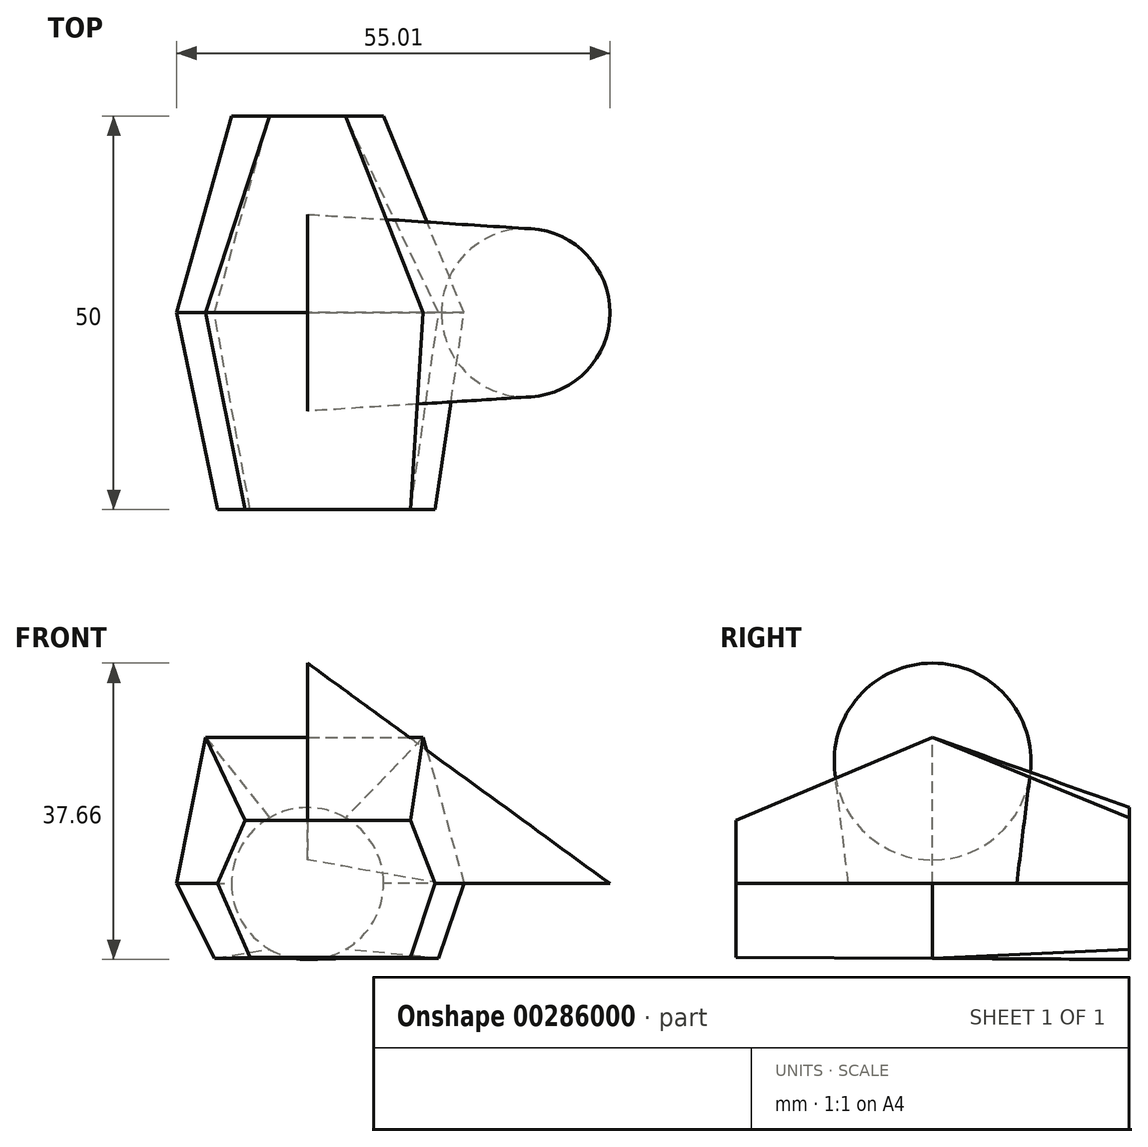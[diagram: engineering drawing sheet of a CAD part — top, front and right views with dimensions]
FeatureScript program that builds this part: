
annotation { "Feature Type Name" : "Feature", "Feature Type Description" : "" }
export const myFeature = defineFeature(function(context is Context, id is Id, definition is map)
    precondition{}
    {
        {
            var Q0;
            Q0=qCreatedBy(makeId("Front.planeOp"),FACE);
            var sketch = newSketch(context, id + "F0", { "sketchPlane" : qUnion([Q0])});
            skLineSegment(sketch, "E0", {"start": v(-16.6, 0) * mm, "end": v(-12.96, 18.58) * mm});
            skLineSegment(sketch, "E1", {"start": v(-12.96, 18.58) * mm, "end": v(14.7, 18.58) * mm});
            skLineSegment(sketch, "E2", {"start": v(14.7, 18.58) * mm, "end": v(19.89, 0) * mm});
            skLineSegment(sketch, "E3", {"start": v(19.89, 0) * mm, "end": v(16.66, -9.5) * mm});
            skLineSegment(sketch, "E4", {"start": v(16.66, -9.5) * mm, "end": v(-11.84, -9.5) * mm});
            skLineSegment(sketch, "E5", {"start": v(-11.84, -9.5) * mm, "end": v(-16.6, 0) * mm});
            skSolve(sketch);
        }
        {
            var Q0;
            Q0=makeQuery(id+"F0.imprint","IMPRINT",FACE,{"disambiguationData":[TD([[makeQuery(id+"F0.imprint","IMPRINT",EDGE,{"derivedFrom":sQuery(id+"F0.wireOp",EDGE,"E0")}),-1.0]])]});
            cPlane(context, id + "F1", {"entities" : qUnion([Q0]), "cplaneType" : CPlaneType.OFFSET, "offset" : 25 * mm, "width" : 150 * mm, "height" : 150 * mm});
        }
        {
            var Q0;
            Q0=makeQuery(id+"F0.imprint","IMPRINT",FACE,{"disambiguationData":[TD([[makeQuery(id+"F0.imprint","IMPRINT",EDGE,{"derivedFrom":sQuery(id+"F0.wireOp",EDGE,"E0")}),-1.0]])]});
            cPlane(context, id + "F2", {"entities" : qUnion([Q0]), "cplaneType" : CPlaneType.OFFSET, "offset" : 25 * mm, "oppositeDirection" : true, "width" : 150 * mm, "height" : 150 * mm});
        }
        {
            var Q0;
            Q0=qCreatedBy(id+"F1.planeOp",FACE);
            var sketch = newSketch(context, id + "F3", { "sketchPlane" : qUnion([Q0])});
            skLineSegment(sketch, "E6", {"start": v(-11.42, 0) * mm, "end": v(-7.96, 8) * mm});
            skLineSegment(sketch, "E7", {"start": v(-7.96, 8) * mm, "end": v(13.1, 8) * mm});
            skLineSegment(sketch, "E8", {"start": v(13.1, 8) * mm, "end": v(16.21, 0) * mm});
            skLineSegment(sketch, "E9", {"start": v(16.21, 0) * mm, "end": v(13.1, -9.38) * mm});
            skLineSegment(sketch, "E10", {"start": v(13.1, -9.38) * mm, "end": v(-7.3, -9.38) * mm});
            skLineSegment(sketch, "E11", {"start": v(-7.3, -9.38) * mm, "end": v(-11.42, 0) * mm});
            skSolve(sketch);
        }
        {
            var Q0;
            Q0=qCreatedBy(id+"F2.planeOp",FACE);
            var sketch = newSketch(context, id + "F4", { "sketchPlane" : qUnion([Q0])});
            skCircle(sketch, "E12", {"center": v(0, 0) * mm, "radius": 9.65 * mm});
            skSolve(sketch);
        }
        {
            var Q0;
            Q0=qCreatedBy(makeId("Right.planeOp"),FACE);
            var sketch = newSketch(context, id + "F5", { "sketchPlane" : qUnion([Q0])});
            skLineSegment(sketch, "E13.0", {"start": v(25, -9.65) * mm, "end": v(25, 9.65) * mm});
            skLineSegment(sketch, "E14.0.0", {"start": v(0, 0) * mm, "end": v(0, -9.5) * mm});
            skLineSegment(sketch, "E14.0.2", {"start": v(0, -9.5) * mm, "end": v(0, 0) * mm});
            skLineSegment(sketch, "E14.0.3", {"start": v(0, 0) * mm, "end": v(0, 18.58) * mm});
            skLineSegment(sketch, "E14.0.5", {"start": v(0, 18.58) * mm, "end": v(0, 0) * mm});
            skLineSegment(sketch, "E15.0.0", {"start": v(-25, 0) * mm, "end": v(-25, -9.38) * mm});
            skLineSegment(sketch, "E15.0.2", {"start": v(-25, -9.38) * mm, "end": v(-25, 0) * mm});
            skLineSegment(sketch, "E15.0.3", {"start": v(-25, 0) * mm, "end": v(-25, 8) * mm});
            skLineSegment(sketch, "E15.0.5", {"start": v(-25, 8) * mm, "end": v(-25, 0) * mm});
            skLineSegment(sketch, "E16", {"start": v(25, -9.65) * mm, "end": v(0, -9.5) * mm});
            skLineSegment(sketch, "E17", {"start": v(25, 9.65) * mm, "end": v(0, 18.58) * mm});
            skLineSegment(sketch, "E18", {"start": v(0, -9.5) * mm, "end": v(-25, -9.38) * mm});
            skLineSegment(sketch, "E19", {"start": v(-25, 8) * mm, "end": v(0, 18.58) * mm});
            skSolve(sketch);
        }
        {
            var Q0;
            Q0=makeQuery(id+"F4.imprint","IMPRINT",FACE,{"disambiguationData":[TD([[makeQuery(id+"F4.imprint","IMPRINT",EDGE,{"derivedFrom":sQuery(id+"F4.wireOp",EDGE,"E12")}),1.0]])]});
            var Q1;
            Q1=makeQuery(id+"F0.imprint","IMPRINT",FACE,{"disambiguationData":[TD([[makeQuery(id+"F0.imprint","IMPRINT",EDGE,{"derivedFrom":sQuery(id+"F0.wireOp",EDGE,"E0")}),-1.0]])]});
            var Q2;
            Q2=sQuery(id+"F5.wireOp",EDGE,"E17");
            var Q3;
            Q3=sQuery(id+"F5.wireOp",EDGE,"E16");
            loft(context, id + "F6", {"sheetProfilesArray" : [{ "sheetProfileEntities" : qUnion([Q0]) }, { "sheetProfileEntities" : qUnion([Q1]) }], "guidesArray" : [{ "guideEntities" : qUnion([Q2]), "guideDerivativeType" : LoftGuideDerivativeType.DEFAULT, "guideDerivativeMagnitude" : 1 }, { "guideEntities" : qUnion([Q3]), "guideDerivativeType" : LoftGuideDerivativeType.DEFAULT, "guideDerivativeMagnitude" : 1 }]});
        }
        {
            var Q1;
            Q1=makeQuery(id+"F3.imprint","IMPRINT",FACE,{"disambiguationData":[TD([[makeQuery(id+"F3.imprint","IMPRINT",EDGE,{"derivedFrom":sQuery(id+"F3.wireOp",EDGE,"E6")}),-1.0]])]});
            var Q2;
            Q2=makeQuery(id+"F6.opLoft","CAP_FACE",FACE,{"disambiguationData":[OSD([makeQuery(id+"F0.imprint","IMPRINT",FACE,{"disambiguationData":[TD([[makeQuery(id+"F0.imprint","IMPRINT",EDGE,{"derivedFrom":sQuery(id+"F0.wireOp",EDGE,"E0")}),-1.0]])]})])],"isStart":true});
            var Q3;
            Q3=sQuery(id+"F5.wireOp",EDGE,"E19");
            var Q4;
            Q4=sQuery(id+"F5.wireOp",EDGE,"E18");
            loft(context, id + "F7", {"addGuides" : true, "sheetProfilesArray" : [{ "sheetProfileEntities" : qUnion([Q1]) }, { "sheetProfileEntities" : qUnion([Q2]) }], "guidesArray" : [{ "guideEntities" : qUnion([Q3]), "guideDerivativeType" : LoftGuideDerivativeType.DEFAULT, "guideDerivativeMagnitude" : 1 }, { "guideEntities" : qUnion([Q4]), "guideDerivativeType" : LoftGuideDerivativeType.DEFAULT, "guideDerivativeMagnitude" : 1 }]});
        }
        {
            var Q0;
            Q0=qCreatedBy(makeId("Right.planeOp"),FACE);
            var sketch = newSketch(context, id + "F8", { "sketchPlane" : qUnion([Q0])});
            skCircle(sketch, "E20", {"center": v(0, 15.5) * mm, "radius": 12.5 * mm});
            skSolve(sketch);
        }
        {
            var Q0;
            Q0=qCreatedBy(makeId("Top.planeOp"),FACE);
            var sketch = newSketch(context, id + "F9", { "sketchPlane" : qUnion([Q0])});
            skCircle(sketch, "E21", {"center": v(27.7, 0) * mm, "radius": 10.7 * mm});
            skSolve(sketch);
        }
        {
            var Q0;
            Q0=qCreatedBy(makeId("Front.planeOp"),FACE);
            var sketch = newSketch(context, id + "F10", { "sketchPlane" : qUnion([Q0])});
            skLineSegment(sketch, "E22.0", {"start": v(0, 28) * mm, "end": v(0, 3) * mm});
            skLineSegment(sketch, "E23.0", {"start": v(17, 0) * mm, "end": v(38.4, 0) * mm});
            skLineSegment(sketch, "E24", {"start": v(0, 3) * mm, "end": v(17, 0) * mm});
            skLineSegment(sketch, "E25", {"start": v(38.4, 0) * mm, "end": v(0, 28) * mm});
            skSolve(sketch);
        }
        {
            var Q0;
            Q0=makeQuery(id+"F8.imprint","IMPRINT",FACE,{"disambiguationData":[TD([[makeQuery(id+"F8.imprint","IMPRINT",EDGE,{"derivedFrom":sQuery(id+"F8.wireOp",EDGE,"E20")}),1.0]])]});
            var Q1;
            Q1=makeQuery(id+"F9.imprint","IMPRINT",FACE,{"disambiguationData":[TD([[makeQuery(id+"F9.imprint","IMPRINT",EDGE,{"derivedFrom":sQuery(id+"F9.wireOp",EDGE,"E21")}),1.0]])]});
            var Q2;
            Q2=sQuery(id+"F10.wireOp",EDGE,"E25");
            var Q3;
            Q3=sQuery(id+"F10.wireOp",EDGE,"E24");
            loft(context, id + "F11", {"addGuides" : true, "sheetProfilesArray" : [{ "sheetProfileEntities" : qUnion([Q0]) }, { "sheetProfileEntities" : qUnion([Q1]) }], "guidesArray" : [{ "guideEntities" : qUnion([Q2]), "guideDerivativeType" : LoftGuideDerivativeType.DEFAULT, "guideDerivativeMagnitude" : 1 }, { "guideEntities" : qUnion([Q3]), "guideDerivativeType" : LoftGuideDerivativeType.DEFAULT, "guideDerivativeMagnitude" : 1 }]});
        }
        {
            var Q0;
            Q0=qCreatedBy(makeId("Top.planeOp"),FACE);
            cPlane(context, id + "F12", {"entities" : qUnion([Q0]), "cplaneType" : CPlaneType.OFFSET, "offset" : 25 * mm, "width" : 150 * mm, "height" : 150 * mm});
        }
        {
            var Q0;
            Q0=makeQuery(id+"F0.imprint","IMPRINT",FACE,{"disambiguationData":[TD([[makeQuery(id+"F0.imprint","IMPRINT",EDGE,{"derivedFrom":sQuery(id+"F0.wireOp",EDGE,"E0")}),-1.0]])]});
            var Q1;
            Q1=makeQuery(id+"F4.imprint","IMPRINT",FACE,{"disambiguationData":[TD([[makeQuery(id+"F4.imprint","IMPRINT",EDGE,{"derivedFrom":sQuery(id+"F4.wireOp",EDGE,"E12")}),1.0]])]});
            loft(context, id + "F13", {"sheetProfilesArray" : [{ "sheetProfileEntities" : qUnion([Q0]) }, { "sheetProfileEntities" : qUnion([Q1]) }]});
        }
    });
